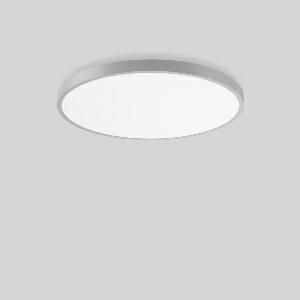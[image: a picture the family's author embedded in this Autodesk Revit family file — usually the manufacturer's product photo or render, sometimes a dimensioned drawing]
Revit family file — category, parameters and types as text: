
# Revit family: triona_round_a_312387_004_2_730_589a
name_source: partatom
category: Lighting Fixtures
units: mm (PartAtom-declared; Revit-internal decimal feet)

## family parameters
Cut with Voids When Loaded = No
Host = Face
Light Source = No
Part Type = Normal
Room Calculation Point = No
Round Connector Dimension = Use Diameter
Shared = No

## types (1)
- TuneableWhite 846 (1 x LED Modul 846, 4800 lm, 4600)
    Apparent Load = 49 VA
    CIE Flux Codes = 50 80 96 100 100
    Color Rendering = 80
    Color Temperature = 4600
    Default Elevation = 1800 mm
    Description = Series: TRIONA round
Decorative round LED surface-mounted luminaire. Flat, seamless frame: aluminium extrusion profile, powder coated. Cover made of sheet steel, powder-coated. Light emission through a diffuser: plastic, opal. Lightguide and diffuser made of non-yellowing plastic (PMMA). Lateral light emission (RZB SIDELITE technology) for above-average homogeneous light distribution. Tunable white versions, dynamically adjustable from 2700 K to 6500 K. Suitable for Ceiling mounting, Wall (surface). Tool-free mounting via bayonet connection. Electronic ballast included. Very easy installation thanks to Plug+Play connection. With Casambi smart+free Bluetooth control for wireless network and operation using Android / iOS devices, free app available for download. Ideal for use as part of the Human Centric Lighting concept in connection with RZB light management systems. 
Colour: silver, matt (approx. RAL 9006)
Diameter: 845 mm
Height: 88 mm
Lamp: LED
Socket: without socket
Colour temperature: 2700K - 6500K
Colour rendering index (CRI): 80
System power: 49 W
Rated luminous flux: 4800 lm
Luminous efficiency: 98 lm/W
System power 2: 51 W
Rated luminous flux 2: 4550 lm
Luminous efficiency 2: 89 lm/W
System power 3: 51 W
Rated luminous flux 3: 4650 lm
Luminous efficiency 3: 91 lm/W
Control gear: Dimmable Bluetooth converter
Protection class: I
Type of protection: IP 20
    Height = 88 mm
    Lamp = 1 x LED Modul 846
    Lamp Light Flux = 4800 lm
    Lamp count = 1
    Length = 845 mm
    Lifetime = 50000 h
    Luminous efficacy = 98 lm/W
    Manufacturer = RZB
    ModVariant = No
    Model = 312387.004.2.730
    Mounting Place = Ceiling
    Mounting Type = Surface mounted
    Number of Poles = 1
    OnlyDefault = Yes
    Power Factor = 1
    Product Name = TRIONA round A
    Product group = Surface mounted modular luminaires
    ProductGroupID = 306
    Protection Class = Protection class I
    Protection Degree = IP 20
    RLX_Detail_Level = 1
    RLX_Emergency_Light_Flux = 0 lm
    RLX_Emergency_Type = 0
    RLX_Emergency_Type_DB = No
    RlxData = <blob elided: 34757 chars, md5=48f36731>
    Socket = socket
    Standby Power = 0 W
    System Light Flux = 4800 lm
    System Power = 49 W
    Type Comments = TuneableWhite 846
    Type Image = 312388.004.jpg
    URL = http://relux.com
    VarID = tuneablewhite_846
    Voltage = 230 V
    Voltage Range = 220-240 V
    Weight = 0.00 kg
    Width = 0 mm  [stored 0 ft]

note: [stored X ft] marks values corroborated as IEEE doubles in the binary element streams (Revit-internal decimal feet)

## geometry (parser evidence)
native form markers: Blend x4, Sweep x8
no freeform markers — native parametric forms only
